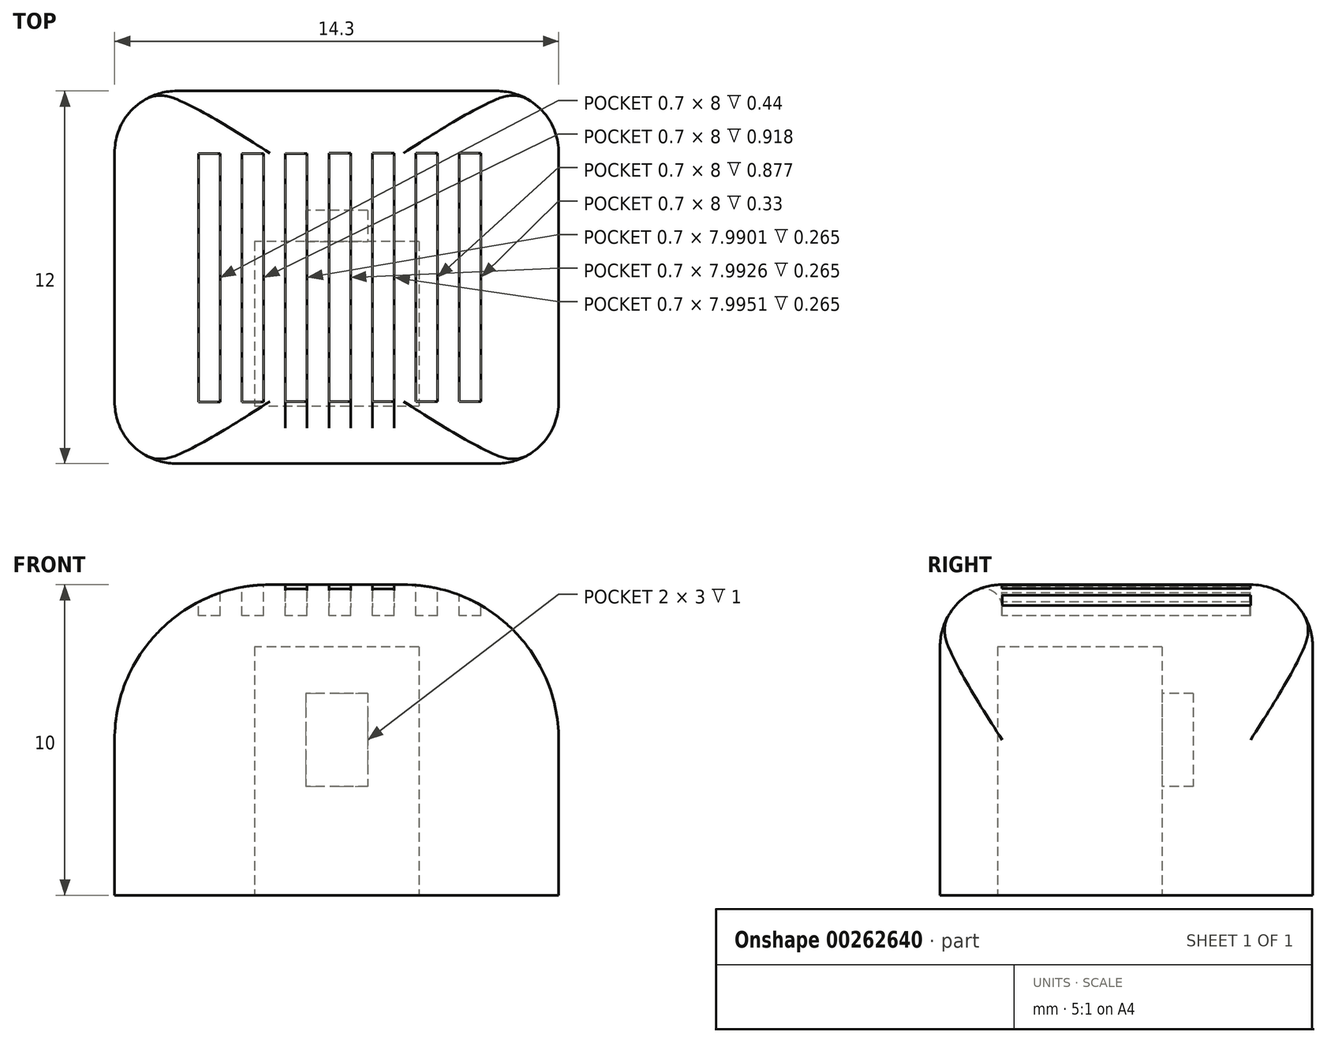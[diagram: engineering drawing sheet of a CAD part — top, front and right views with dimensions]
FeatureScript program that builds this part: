
annotation { "Feature Type Name" : "Feature", "Feature Type Description" : "" }
export const myFeature = defineFeature(function(context is Context, id is Id, definition is map)
    precondition{}
    {
        {
            var Q0;
            Q0=qCreatedBy(makeId("Top.planeOp"),FACE);
            var sketch = newSketch(context, id + "F0", { "sketchPlane" : qUnion([Q0])});
            skLineSegment(sketch, "E0", {"start": v(0, 0) * mm, "end": v(-7.15, 0) * mm});
            skLineSegment(sketch, "E1", {"start": v(-7.15, 0) * mm, "end": v(-7.15, 12) * mm});
            skLineSegment(sketch, "E2", {"start": v(-7.15, 12) * mm, "end": v(0, 12) * mm});
            skLineSegment(sketch, "E3", {"start": v(0, 8.15) * mm, "end": v(-1, 8.15) * mm});
            skLineSegment(sketch, "E4", {"start": v(-1, 8.15) * mm, "end": v(-1, 7.15) * mm});
            skLineSegment(sketch, "E5", {"start": v(-1, 7.15) * mm, "end": v(-2.65, 7.15) * mm});
            skLineSegment(sketch, "E6", {"start": v(-2.65, 7.15) * mm, "end": v(-2.65, 1.85) * mm});
            skLineSegment(sketch, "E7", {"start": v(-2.65, 1.85) * mm, "end": v(0, 1.85) * mm});
            skLineSegment(sketch, "E8", {"start": v(0, 12) * mm, "end": v(0, 8.15) * mm});
            skLineSegment(sketch, "E9", {"start": v(0, 1.85) * mm, "end": v(0, 8.15) * mm});
            skLineSegment(sketch, "E10", {"start": v(0, 1.85) * mm, "end": v(0, 0) * mm});
            skLineSegment(sketch, "E11", {"start": v(-1, 7.15) * mm, "end": v(0, 7.15) * mm});
            skSolve(sketch);
        }
        {
            var Q0;
            Q0=makeQuery(id+"F0.imprint","IMPRINT",FACE,{"disambiguationData":[TD([[makeQuery(id+"F0.imprint","IMPRINT",EDGE,{"derivedFrom":sQuery(id+"F0.wireOp",EDGE,"E0")}),-1.0]])]});
            var Q1;
            {var subQ2=sQuery(id+"F0.wireOp",EDGE,"E3");Q1=makeQuery(id+"F0.imprint","IMPRINT",FACE,{"disambiguationData":[TD([[makeQuery(id+"F0.imprint","IMPRINT",EDGE,{"derivedFrom":subQ2}),1.0]])]});}
            var Q2;
            Q2=makeQuery(id+"F0.imprint","IMPRINT",FACE,{"disambiguationData":[TD([[makeQuery(id+"F0.imprint","IMPRINT",EDGE,{"derivedFrom":sQuery(id+"F0.wireOp",EDGE,"E5")}),1.0]])]});
            extrude(context, id + "F1", {"entities" : qUnion([Q0, Q1, Q2]), "depth" : 10 * mm});
        }
        {
            var Q0;
            {var subQ2=sQuery(id+"F0.wireOp",EDGE,"E3");Q0=makeQuery(id+"F0.imprint","IMPRINT",FACE,{"disambiguationData":[TD([[makeQuery(id+"F0.imprint","IMPRINT",EDGE,{"derivedFrom":subQ2}),1.0]])]});}
            var Q1;
            Q1=makeQuery(id+"F0.imprint","IMPRINT",FACE,{"disambiguationData":[TD([[makeQuery(id+"F0.imprint","IMPRINT",EDGE,{"derivedFrom":sQuery(id+"F0.wireOp",EDGE,"E5")}),1.0]])]});
            extrude(context, id + "F2", {"entities" : qUnion([Q0, Q1]), "operationType" : NewBodyOperationType.REMOVE, "depth" : 8 * mm});
        }
        {
            var Q0;
            Q0=makeQuery(id+"F1.opExtrude","SWEPT_EDGE",EDGE,{"disambiguationData":[OSD([sQuery(id+"F0.wireOp",EDGE,"E0"),sQuery(id+"F0.wireOp",EDGE,"E1")])]});
            var Q1;
            Q1=makeQuery(id+"F1.opExtrude","CAP_EDGE",EDGE,{"disambiguationData":[OSD([sQuery(id+"F0.wireOp",EDGE,"E1")])],"isStart":false});
            var Q2;
            Q2=makeQuery(id+"F1.opExtrude","CAP_EDGE",EDGE,{"disambiguationData":[OSD([sQuery(id+"F0.wireOp",EDGE,"E0")])],"isStart":false});
            var Q3;
            Q3=makeQuery(id+"F1.opExtrude","CAP_EDGE",EDGE,{"disambiguationData":[OSD([sQuery(id+"F0.wireOp",EDGE,"E2")])],"isStart":false});
            var Q4;
            Q4=makeQuery(id+"F1.opExtrude","SWEPT_EDGE",EDGE,{"disambiguationData":[OSD([sQuery(id+"F0.wireOp",EDGE,"E1"),sQuery(id+"F0.wireOp",EDGE,"E2")])]});
            fillet(context, id + "F3", {"entities" : qUnion([Q0, Q1, Q2, Q3, Q4]), "radius" : 2 * mm, "tangentPropagation" : true, "allowEdgeOverflow" : false});
        }
        {
            var Q0;
            Q0=makeQuery(id+"F1.opExtrude","SWEPT_BODY",BODY,{"disambiguationData":[OSD([sQuery(id+"F0.wireOp",EDGE,"E0"),sQuery(id+"F0.wireOp",EDGE,"E1"),sQuery(id+"F0.wireOp",EDGE,"E2"),sQuery(id+"F0.wireOp",EDGE,"E8"),sQuery(id+"F0.wireOp",EDGE,"E9"),sQuery(id+"F0.wireOp",EDGE,"E10")])]});
            var Q1;
            Q1=qCreatedBy(makeId("Right.planeOp"),FACE);
            mirror(context, id + "F4", {"entities" : qUnion([Q0]), "mirrorPlane" : qUnion([Q1])});
        }
        {
            var Q0;
            Q0=makeQuery(id+"F1.opExtrude","SWEPT_BODY",BODY,{"disambiguationData":[OSD([sQuery(id+"F0.wireOp",EDGE,"E0"),sQuery(id+"F0.wireOp",EDGE,"E1"),sQuery(id+"F0.wireOp",EDGE,"E2"),sQuery(id+"F0.wireOp",EDGE,"E8"),sQuery(id+"F0.wireOp",EDGE,"E9"),sQuery(id+"F0.wireOp",EDGE,"E10")])]});
            var Q1;
            Q1=makeQuery(id+"F4.opPattern","COPY",BODY,{"derivedFrom":makeQuery(id+"F1.opExtrude","SWEPT_BODY",BODY,{"disambiguationData":[OSD([sQuery(id+"F0.wireOp",EDGE,"E0"),sQuery(id+"F0.wireOp",EDGE,"E1"),sQuery(id+"F0.wireOp",EDGE,"E2"),sQuery(id+"F0.wireOp",EDGE,"E8"),sQuery(id+"F0.wireOp",EDGE,"E9"),sQuery(id+"F0.wireOp",EDGE,"E10")])]}),"instanceName":"1"});
            booleanBodies(context, id + "F5", {"operationType" : BooleanOperationType.UNION, "tools" : qUnion([Q0, Q1])});
        }
        {
            var Q0;
            Q0=makeQuery(id+"F2.boolean.opBoolean","COPY",FACE,{"derivedFrom":makeQuery(id+"F2.opExtrude","SWEPT_FACE",FACE,{"disambiguationData":[OSD([sQuery(id+"F0.wireOp",EDGE,"E5")])]})});
            var sketch = newSketch(context, id + "F6", { "sketchPlane" : qUnion([Q0])});
            skLineSegment(sketch, "E12.0.0", {"start": v(1, 0) * mm, "end": v(-1, 0) * mm});
            skLineSegment(sketch, "E12.0.1", {"start": v(1, 8) * mm, "end": v(1, 0) * mm});
            skLineSegment(sketch, "E12.0.2", {"start": v(1, 8) * mm, "end": v(-1, 8) * mm});
            skLineSegment(sketch, "E12.0.3", {"start": v(-1, 8) * mm, "end": v(-1, 0) * mm});
            skLineSegment(sketch, "E13.bottom", {"start": v(-1, 6.5) * mm, "end": v(1, 6.5) * mm});
            skLineSegment(sketch, "E13.top", {"start": v(-1, 3.5) * mm, "end": v(1, 3.5) * mm});
            skLineSegment(sketch, "E13.left", {"start": v(-1, 6.5) * mm, "end": v(-1, 3.5) * mm});
            skLineSegment(sketch, "E13.right", {"start": v(1, 6.5) * mm, "end": v(1, 3.5) * mm});
            skSolve(sketch);
        }
        {
            var Q0;
            {var subQ0=makeQuery(id+"F1.opExtrude","SWEPT_FACE",FACE,{"disambiguationData":[OSD([sQuery(id+"F0.wireOp",EDGE,"E0")])]});Q0=makeQuery(id+"F5.opBoolean","MERGE",FACE,{"derivedFrom":[subQ0,makeQuery(id+"F4.opPattern","COPY",FACE,{"derivedFrom":subQ0,"instanceName":"1"})]});}
            var sketch = newSketch(context, id + "F7", { "sketchPlane" : qUnion([Q0])});
            skLineSegment(sketch, "E14.0", {"start": v(-7.15, 8) * mm, "end": v(-6.15, 8) * mm});
            skLineSegment(sketch, "E15.0", {"start": v(-7.15, 0) * mm, "end": v(-7.15, 5) * mm});
            skLineSegment(sketch, "E16.0.0", {"start": v(5.15, 0) * mm, "end": v(7.15, 0) * mm});
            skLineSegment(sketch, "E16.0.1", {"start": v(7.15, 0) * mm, "end": v(7.15, 8) * mm});
            skLineSegment(sketch, "E16.0.2", {"start": v(7.15, 8) * mm, "end": v(6.15, 8) * mm});
            skLineSegment(sketch, "E17.0", {"start": v(5.15, 9) * mm, "end": v(5.15, 10) * mm});
            skLineSegment(sketch, "E18.0", {"start": v(-5.15, 9) * mm, "end": v(-5.15, 10) * mm});
            skLineSegment(sketch, "E19", {"start": v(-2.15, 10) * mm, "end": v(5.15, 10) * mm});
            skLineSegment(sketch, "E20", {"start": v(5.15, 10) * mm, "end": v(7.15, 10) * mm});
            skLineSegment(sketch, "E21", {"start": v(7.15, 10) * mm, "end": v(7.15, 8) * mm});
            skLineSegment(sketch, "E22", {"start": v(-7.15, 8) * mm, "end": v(-7.15, 10) * mm});
            skLineSegment(sketch, "E23", {"start": v(-7.15, 10) * mm, "end": v(-5.15, 10) * mm});
            skArc(sketch, "E24.filletArc", {"start": v(-2.15, 10) * mm, "mid": v(-5.69, 8.54) * mm, "end": v(-7.15, 5) * mm});
            skArc(sketch, "E25.0.MirrorCS", {"start": v(2.15, 10) * mm, "mid": v(5.69, 8.54) * mm, "end": v(7.15, 5) * mm});
            skPoint(sketch, "E26.0.end.orphan", {"position": v(-5.15, 8) * mm});
            skPoint(sketch, "E27.orphan", {"position": v(5.15, 8) * mm});
            skLineSegment(sketch, "E28", {"start": v(-7.15, 0) * mm, "end": v(5.15, 0) * mm});
            skPoint(sketch, "E29.start.orphan", {"position": v(0, 0) * mm});
            skSolve(sketch);
        }
        {
            var Q0;
            {var subQ5=sQuery(id+"F7.wireOp",EDGE,"E15.0");Q0=makeQuery(id+"F7.imprint","IMPRINT",FACE,{"disambiguationData":[TD([[makeQuery(id+"F7.imprint","IMPRINT",EDGE,{"derivedFrom":subQ5}),-1.0]])]});}
            var Q1;
            {var subQ0=sQuery(id+"F0.wireOp",EDGE,"E0");var subQ1=makeQuery(id+"F1.opExtrude","SWEPT_FACE",FACE,{"disambiguationData":[OSD([subQ0])]});var subQ3=makeQuery(id+"F3.opFillet","BLEND_EDGE",EDGE,{"blendedFrom":[makeQuery(id+"F1.opExtrude","SWEPT_EDGE",EDGE,{"disambiguationData":[OSD([subQ0,sQuery(id+"F0.wireOp",EDGE,"E1")])]}),subQ1],"blendedInto":[subQ1]});Q1=makeQuery(id+"F7.imprint","IMPRINT",FACE,{"disambiguationData":[TD([[makeQuery(id+"F7.imprint","IMPRINT",EDGE,{"derivedFrom":subQ3}),1.0]])]});}
            extrude(context, id + "F8", {"entities" : qUnion([Q0, Q1]), "operationType" : NewBodyOperationType.INTERSECT, "oppositeDirection" : true, "depth" : 25 * mm});
        }
        {
            var Q0;
            {var subQ2=sQuery(id+"F6.wireOp",EDGE,"E12.0.0");Q0=makeQuery(id+"F6.imprint","IMPRINT",FACE,{"disambiguationData":[TD([[makeQuery(id+"F6.imprint","IMPRINT",EDGE,{"derivedFrom":subQ2}),-1.0]])]});}
            var Q1;
            {var subQ2=sQuery(id+"F6.wireOp",EDGE,"E12.0.2");Q1=makeQuery(id+"F6.imprint","IMPRINT",FACE,{"disambiguationData":[TD([[makeQuery(id+"F6.imprint","IMPRINT",EDGE,{"derivedFrom":subQ2}),1.0]])]});}
            var Q2;
            {var subQ0=makeQuery(id+"F2.boolean.opBoolean","COPY",FACE,{"derivedFrom":makeQuery(id+"F2.opExtrude","SWEPT_FACE",FACE,{"disambiguationData":[OSD([sQuery(id+"F0.wireOp",EDGE,"E3")])]})});Q2=makeQuery(id+"F5.opBoolean","MERGE",FACE,{"derivedFrom":[subQ0,makeQuery(id+"F4.opPattern","COPY",FACE,{"derivedFrom":subQ0,"instanceName":"1"})]});}
            extrude(context, id + "F9", {"entities" : qUnion([Q0, Q1]), "operationType" : NewBodyOperationType.ADD, "endBound" : BoundingType.UP_TO_SURFACE, "oppositeDirection" : true, "endBoundEntityFace" : qUnion([Q2]), "depth" : 25 * mm});
        }
        {
            var Q0;
            {var subQ0=makeQuery(id+"F1.opExtrude","CAP_FACE",FACE,{"disambiguationData":[OSD([sQuery(id+"F0.wireOp",EDGE,"E0"),sQuery(id+"F0.wireOp",EDGE,"E1"),sQuery(id+"F0.wireOp",EDGE,"E2"),sQuery(id+"F0.wireOp",EDGE,"E8"),sQuery(id+"F0.wireOp",EDGE,"E9"),sQuery(id+"F0.wireOp",EDGE,"E10")])],"isStart":false});Q0=makeQuery(id+"F5.opBoolean","MERGE",FACE,{"derivedFrom":[subQ0,makeQuery(id+"F4.opPattern","COPY",FACE,{"derivedFrom":subQ0,"instanceName":"1"})]});}
            var sketch = newSketch(context, id + "F10", { "sketchPlane" : qUnion([Q0])});
            skLineSegment(sketch, "E30.0.MirrorCS", {"start": v(3.95, 10) * mm, "end": v(3.95, 2) * mm});
            skLineSegment(sketch, "E31.0.MirrorCS", {"start": v(4.65, 10) * mm, "end": v(4.65, 2) * mm});
            skLineSegment(sketch, "E32", {"start": v(4.65, 10) * mm, "end": v(3.95, 10) * mm});
            skLineSegment(sketch, "E33", {"start": v(4.65, 2) * mm, "end": v(3.95, 2) * mm});
            skLineSegment(sketch, "E34.1.0.0", {"start": v(3.25, 2) * mm, "end": v(2.55, 2) * mm});
            skLineSegment(sketch, "E34.1.0.1", {"start": v(3.25, 10) * mm, "end": v(3.25, 2) * mm});
            skLineSegment(sketch, "E34.1.0.2", {"start": v(2.55, 10) * mm, "end": v(2.55, 2) * mm});
            skLineSegment(sketch, "E34.1.0.3", {"start": v(3.25, 10) * mm, "end": v(2.55, 10) * mm});
            skLineSegment(sketch, "E34.2.0.0", {"start": v(1.85, 2) * mm, "end": v(1.15, 2) * mm});
            skLineSegment(sketch, "E34.2.0.1", {"start": v(1.85, 10) * mm, "end": v(1.85, 2) * mm});
            skLineSegment(sketch, "E34.2.0.2", {"start": v(1.15, 10) * mm, "end": v(1.15, 2) * mm});
            skLineSegment(sketch, "E34.2.0.3", {"start": v(1.85, 10) * mm, "end": v(1.15, 10) * mm});
            skLineSegment(sketch, "E34.3.0.0", {"start": v(0.45, 2) * mm, "end": v(-0.25, 2) * mm});
            skLineSegment(sketch, "E34.3.0.1", {"start": v(0.45, 10) * mm, "end": v(0.45, 2) * mm});
            skLineSegment(sketch, "E34.3.0.2", {"start": v(-0.25, 10) * mm, "end": v(-0.25, 2) * mm});
            skLineSegment(sketch, "E34.3.0.3", {"start": v(0.45, 10) * mm, "end": v(-0.25, 10) * mm});
            skLineSegment(sketch, "E34.4.0.0", {"start": v(-0.95, 2) * mm, "end": v(-1.65, 2) * mm});
            skLineSegment(sketch, "E34.4.0.1", {"start": v(-0.95, 10) * mm, "end": v(-0.95, 2) * mm});
            skLineSegment(sketch, "E34.4.0.2", {"start": v(-1.65, 10) * mm, "end": v(-1.65, 2) * mm});
            skLineSegment(sketch, "E34.4.0.3", {"start": v(-0.95, 10) * mm, "end": v(-1.65, 10) * mm});
            skLineSegment(sketch, "E34.5.0.0", {"start": v(-2.35, 1.99) * mm, "end": v(-3.05, 1.99) * mm});
            skLineSegment(sketch, "E34.5.0.1", {"start": v(-2.35, 9.99) * mm, "end": v(-2.35, 1.99) * mm});
            skLineSegment(sketch, "E34.5.0.2", {"start": v(-3.05, 9.99) * mm, "end": v(-3.05, 1.99) * mm});
            skLineSegment(sketch, "E34.5.0.3", {"start": v(-2.35, 9.99) * mm, "end": v(-3.05, 9.99) * mm});
            skLineSegment(sketch, "E34.6.0.0", {"start": v(-3.75, 1.99) * mm, "end": v(-4.45, 1.99) * mm});
            skLineSegment(sketch, "E34.6.0.1", {"start": v(-3.75, 9.99) * mm, "end": v(-3.75, 1.99) * mm});
            skLineSegment(sketch, "E34.6.0.2", {"start": v(-4.45, 9.99) * mm, "end": v(-4.45, 1.99) * mm});
            skLineSegment(sketch, "E34.6.0.3", {"start": v(-3.75, 9.99) * mm, "end": v(-4.45, 9.99) * mm});
            skLineSegment(sketch, "E34.direction1", {"start": v(3.95, 2) * mm, "end": v(2.55, 2) * mm, "construction": true});
            skSolve(sketch);
        }
        {
            var Q0;
            Q0=makeQuery(id+"F10.imprint","IMPRINT",FACE,{"disambiguationData":[TD([[makeQuery(id+"F10.imprint","IMPRINT",EDGE,{"derivedFrom":sQuery(id+"F10.wireOp",EDGE,"E30.0.MirrorCS")}),1.0]])]});
            var Q1;
            Q1=makeQuery(id+"F10.imprint","IMPRINT",FACE,{"disambiguationData":[TD([[makeQuery(id+"F10.imprint","IMPRINT",EDGE,{"derivedFrom":sQuery(id+"F10.wireOp",EDGE,"E34.1.0.0")}),-1.0]])]});
            var Q2;
            {var subQ0=sQuery(id+"F10.wireOp",EDGE,"E34.2.0.3");Q2=makeQuery(id+"F10.imprint","IMPRINT",FACE,{"disambiguationData":[TD([[makeQuery(id+"F10.imprint","IMPRINT",EDGE,{"derivedFrom":subQ0}),1.0]])]});}
            var Q3;
            {var subQ0=sQuery(id+"F10.wireOp",EDGE,"E34.3.0.3");Q3=makeQuery(id+"F10.imprint","IMPRINT",FACE,{"disambiguationData":[TD([[makeQuery(id+"F10.imprint","IMPRINT",EDGE,{"derivedFrom":subQ0}),1.0]])]});}
            var Q4;
            {var subQ0=sQuery(id+"F10.wireOp",EDGE,"E34.4.0.3");Q4=makeQuery(id+"F10.imprint","IMPRINT",FACE,{"disambiguationData":[TD([[makeQuery(id+"F10.imprint","IMPRINT",EDGE,{"derivedFrom":subQ0}),1.0]])]});}
            var Q5;
            Q5=makeQuery(id+"F10.imprint","IMPRINT",FACE,{"disambiguationData":[TD([[makeQuery(id+"F10.imprint","IMPRINT",EDGE,{"derivedFrom":sQuery(id+"F10.wireOp",EDGE,"E34.5.0.0")}),-1.0]])]});
            var Q6;
            Q6=makeQuery(id+"F10.imprint","IMPRINT",FACE,{"disambiguationData":[TD([[makeQuery(id+"F10.imprint","IMPRINT",EDGE,{"derivedFrom":sQuery(id+"F10.wireOp",EDGE,"E34.6.0.0")}),-1.0]])]});
            extrude(context, id + "F11", {"entities" : qUnion([Q0, Q1, Q2, Q3, Q4, Q5, Q6]), "operationType" : NewBodyOperationType.REMOVE, "oppositeDirection" : true, "depth" : 1 * mm});
        }
        {
            var Q0;
            Q0=makeQuery(id+"F11.boolean.opBoolean","INTERSECT",EDGE,{"derivedFrom":[makeQuery(id+"F8.boolean.opBoolean","COPY",FACE,{"derivedFrom":makeQuery(id+"F8.boolean.toolComplement.opBoolean","COPY",FACE,{"derivedFrom":makeQuery(id+"F8.opExtrude","SWEPT_FACE",FACE,{"disambiguationData":[OSD([sQuery(id+"F7.wireOp",EDGE,"E24.filletArc")])]})})}),makeQuery(id+"F11.opExtrude","SWEPT_FACE",FACE,{"disambiguationData":[OSD([sQuery(id+"F10.wireOp",EDGE,"E34.6.0.2")])]})]});
            var Q1;
            Q1=makeQuery(id+"F11.boolean.opBoolean","INTERSECT",EDGE,{"derivedFrom":[makeQuery(id+"F8.boolean.opBoolean","COPY",FACE,{"derivedFrom":makeQuery(id+"F8.boolean.toolComplement.opBoolean","COPY",FACE,{"derivedFrom":makeQuery(id+"F8.opExtrude","SWEPT_FACE",FACE,{"disambiguationData":[OSD([sQuery(id+"F7.wireOp",EDGE,"E24.filletArc")])]})})}),makeQuery(id+"F11.opExtrude","SWEPT_FACE",FACE,{"disambiguationData":[OSD([sQuery(id+"F10.wireOp",EDGE,"E34.5.0.2")])]})]});
            var Q2;
            Q2=makeQuery(id+"F11.boolean.opBoolean","COPY",EDGE,{"derivedFrom":makeQuery(id+"F11.opExtrude","CAP_EDGE",EDGE,{"disambiguationData":[OSD([sQuery(id+"F10.wireOp",EDGE,"E34.4.0.2")])],"isStart":true})});
            var Q3;
            Q3=makeQuery(id+"F11.boolean.opBoolean","COPY",EDGE,{"derivedFrom":makeQuery(id+"F11.opExtrude","CAP_EDGE",EDGE,{"disambiguationData":[OSD([sQuery(id+"F10.wireOp",EDGE,"E34.3.0.2")])],"isStart":true})});
            var Q4;
            Q4=makeQuery(id+"F11.boolean.opBoolean","COPY",EDGE,{"derivedFrom":makeQuery(id+"F11.opExtrude","CAP_EDGE",EDGE,{"disambiguationData":[OSD([sQuery(id+"F10.wireOp",EDGE,"E34.2.0.2")])],"isStart":true})});
            var Q5;
            Q5=makeQuery(id+"F11.boolean.opBoolean","INTERSECT",EDGE,{"derivedFrom":[makeQuery(id+"F8.boolean.opBoolean","COPY",FACE,{"derivedFrom":makeQuery(id+"F8.boolean.toolComplement.opBoolean","COPY",FACE,{"derivedFrom":makeQuery(id+"F8.opExtrude","SWEPT_FACE",FACE,{"disambiguationData":[OSD([sQuery(id+"F7.wireOp",EDGE,"E25.0.MirrorCS")])]})})}),makeQuery(id+"F11.opExtrude","SWEPT_FACE",FACE,{"disambiguationData":[OSD([sQuery(id+"F10.wireOp",EDGE,"E34.1.0.2")])]})]});
            var Q6;
            Q6=makeQuery(id+"F11.boolean.opBoolean","INTERSECT",EDGE,{"derivedFrom":[makeQuery(id+"F8.boolean.opBoolean","COPY",FACE,{"derivedFrom":makeQuery(id+"F8.boolean.toolComplement.opBoolean","COPY",FACE,{"derivedFrom":makeQuery(id+"F8.opExtrude","SWEPT_FACE",FACE,{"disambiguationData":[OSD([sQuery(id+"F7.wireOp",EDGE,"E25.0.MirrorCS")])]})})}),makeQuery(id+"F11.opExtrude","SWEPT_FACE",FACE,{"disambiguationData":[OSD([sQuery(id+"F10.wireOp",EDGE,"E30.0.MirrorCS")])]})]});
            var Q7;
            Q7=makeQuery(id+"F11.boolean.opBoolean","INTERSECT",EDGE,{"derivedFrom":[makeQuery(id+"F8.boolean.opBoolean","COPY",FACE,{"derivedFrom":makeQuery(id+"F8.boolean.toolComplement.opBoolean","COPY",FACE,{"derivedFrom":makeQuery(id+"F8.opExtrude","SWEPT_FACE",FACE,{"disambiguationData":[OSD([sQuery(id+"F7.wireOp",EDGE,"E25.0.MirrorCS")])]})})}),makeQuery(id+"F11.opExtrude","SWEPT_FACE",FACE,{"disambiguationData":[OSD([sQuery(id+"F10.wireOp",EDGE,"E31.0.MirrorCS")])]})]});
            var Q8;
            Q8=makeQuery(id+"F11.boolean.opBoolean","INTERSECT",EDGE,{"derivedFrom":[makeQuery(id+"F8.boolean.opBoolean","COPY",FACE,{"derivedFrom":makeQuery(id+"F8.boolean.toolComplement.opBoolean","COPY",FACE,{"derivedFrom":makeQuery(id+"F8.opExtrude","SWEPT_FACE",FACE,{"disambiguationData":[OSD([sQuery(id+"F7.wireOp",EDGE,"E25.0.MirrorCS")])]})})}),makeQuery(id+"F11.opExtrude","SWEPT_FACE",FACE,{"disambiguationData":[OSD([sQuery(id+"F10.wireOp",EDGE,"E34.1.0.1")])]})]});
            var Q9;
            Q9=makeQuery(id+"F11.boolean.opBoolean","COPY",EDGE,{"derivedFrom":makeQuery(id+"F11.opExtrude","CAP_EDGE",EDGE,{"disambiguationData":[OSD([sQuery(id+"F10.wireOp",EDGE,"E34.2.0.1")])],"isStart":true})});
            var Q10;
            Q10=makeQuery(id+"F11.boolean.opBoolean","COPY",EDGE,{"derivedFrom":makeQuery(id+"F11.opExtrude","CAP_EDGE",EDGE,{"disambiguationData":[OSD([sQuery(id+"F10.wireOp",EDGE,"E34.3.0.1")])],"isStart":true})});
            var Q11;
            Q11=makeQuery(id+"F11.boolean.opBoolean","COPY",EDGE,{"derivedFrom":makeQuery(id+"F11.opExtrude","CAP_EDGE",EDGE,{"disambiguationData":[OSD([sQuery(id+"F10.wireOp",EDGE,"E34.4.0.1")])],"isStart":true})});
            var Q12;
            Q12=makeQuery(id+"F11.boolean.opBoolean","INTERSECT",EDGE,{"derivedFrom":[makeQuery(id+"F8.boolean.opBoolean","COPY",FACE,{"derivedFrom":makeQuery(id+"F8.boolean.toolComplement.opBoolean","COPY",FACE,{"derivedFrom":makeQuery(id+"F8.opExtrude","SWEPT_FACE",FACE,{"disambiguationData":[OSD([sQuery(id+"F7.wireOp",EDGE,"E24.filletArc")])]})})}),makeQuery(id+"F11.opExtrude","SWEPT_FACE",FACE,{"disambiguationData":[OSD([sQuery(id+"F10.wireOp",EDGE,"E34.5.0.1")])]})]});
            var Q13;
            Q13=makeQuery(id+"F8.boolean.opBoolean","COPY",FACE,{"derivedFrom":makeQuery(id+"F8.boolean.toolComplement.opBoolean","COPY",FACE,{"derivedFrom":makeQuery(id+"F8.opExtrude","SWEPT_FACE",FACE,{"disambiguationData":[OSD([sQuery(id+"F7.wireOp",EDGE,"E24.filletArc")])]})})});
            var Q14;
            Q14=makeQuery(id+"F11.boolean.opBoolean","COPY",EDGE,{"derivedFrom":makeQuery(id+"F11.opExtrude","CAP_EDGE",EDGE,{"disambiguationData":[OSD([sQuery(id+"F10.wireOp",EDGE,"E34.4.0.3")])],"isStart":true})});
            var Q15;
            {var subQ0=sQuery(id+"F0.wireOp",EDGE,"E10");var subQ1=sQuery(id+"F0.wireOp",EDGE,"E9");var subQ2=sQuery(id+"F0.wireOp",EDGE,"E8");var subQ3=sQuery(id+"F0.wireOp",EDGE,"E2");var subQ4=sQuery(id+"F0.wireOp",EDGE,"E1");var subQ5=sQuery(id+"F0.wireOp",EDGE,"E0");var subQ6=makeQuery(id+"F3.opFillet","BLEND_EDGE",EDGE,{"blendedFrom":[makeQuery(id+"F1.opExtrude","CAP_EDGE",EDGE,{"disambiguationData":[OSD([subQ5])],"isStart":false}),makeQuery(id+"F1.opExtrude","CAP_FACE",FACE,{"disambiguationData":[OSD([subQ5,subQ4,subQ3,subQ2,subQ1,subQ0])],"isStart":false})],"blendedInto":[makeQuery(id+"F1.opExtrude","CAP_FACE",FACE,{"disambiguationData":[OSD([subQ5,subQ4,subQ3,subQ2,subQ1,subQ0])],"isStart":false})]});var subQ7=makeQuery(id+"F5.opBoolean","MERGE",EDGE,{"derivedFrom":[subQ6,makeQuery(id+"F4.opPattern","COPY",EDGE,{"derivedFrom":subQ6,"instanceName":"1"})]});Q15=makeQuery(id+"F11.boolean.opBoolean","MERGE",EDGE,{"derivedFrom":[subQ7,makeQuery(id+"F11.opExtrude","CAP_EDGE",EDGE,{"disambiguationData":[OSD([subQ5,subQ4,subQ3,subQ2,subQ1,subQ0]),TDD([makeQuery(id+"F10.imprint","IMPRINT",EDGE,{"disambiguationData":[TD([[makeQuery(id+"F10.imprint","INTERSECT",VERTEX,{"derivedFrom":[subQ7,sQuery(id+"F10.wireOp",EDGE,"E34.4.0.1")]}),1.0]])],"derivedFrom":subQ7})])],"isStart":true})]});}
            var Q16;
            {var subQ0=sQuery(id+"F0.wireOp",EDGE,"E10");var subQ1=sQuery(id+"F0.wireOp",EDGE,"E9");var subQ2=sQuery(id+"F0.wireOp",EDGE,"E8");var subQ3=sQuery(id+"F0.wireOp",EDGE,"E2");var subQ4=sQuery(id+"F0.wireOp",EDGE,"E1");var subQ5=sQuery(id+"F0.wireOp",EDGE,"E0");var subQ6=makeQuery(id+"F3.opFillet","BLEND_EDGE",EDGE,{"blendedFrom":[makeQuery(id+"F1.opExtrude","CAP_EDGE",EDGE,{"disambiguationData":[OSD([subQ5])],"isStart":false}),makeQuery(id+"F1.opExtrude","CAP_FACE",FACE,{"disambiguationData":[OSD([subQ5,subQ4,subQ3,subQ2,subQ1,subQ0])],"isStart":false})],"blendedInto":[makeQuery(id+"F1.opExtrude","CAP_FACE",FACE,{"disambiguationData":[OSD([subQ5,subQ4,subQ3,subQ2,subQ1,subQ0])],"isStart":false})]});var subQ7=makeQuery(id+"F5.opBoolean","MERGE",EDGE,{"derivedFrom":[subQ6,makeQuery(id+"F4.opPattern","COPY",EDGE,{"derivedFrom":subQ6,"instanceName":"1"})]});Q16=makeQuery(id+"F11.boolean.opBoolean","MERGE",EDGE,{"derivedFrom":[subQ7,makeQuery(id+"F11.opExtrude","CAP_EDGE",EDGE,{"disambiguationData":[OSD([subQ5,subQ4,subQ3,subQ2,subQ1,subQ0]),TDD([makeQuery(id+"F10.imprint","IMPRINT",EDGE,{"disambiguationData":[TD([[makeQuery(id+"F10.imprint","INTERSECT",VERTEX,{"derivedFrom":[subQ7,sQuery(id+"F10.wireOp",EDGE,"E34.3.0.1")]}),1.0]])],"derivedFrom":subQ7})])],"isStart":true})]});}
            var Q17;
            Q17=makeQuery(id+"F11.boolean.opBoolean","COPY",EDGE,{"derivedFrom":makeQuery(id+"F11.opExtrude","CAP_EDGE",EDGE,{"disambiguationData":[OSD([sQuery(id+"F10.wireOp",EDGE,"E34.3.0.3")])],"isStart":true})});
            var Q18;
            Q18=makeQuery(id+"F11.boolean.opBoolean","COPY",EDGE,{"derivedFrom":makeQuery(id+"F11.opExtrude","CAP_EDGE",EDGE,{"disambiguationData":[OSD([sQuery(id+"F10.wireOp",EDGE,"E34.2.0.3")])],"isStart":true})});
            var Q19;
            {var subQ0=sQuery(id+"F0.wireOp",EDGE,"E10");var subQ1=sQuery(id+"F0.wireOp",EDGE,"E9");var subQ2=sQuery(id+"F0.wireOp",EDGE,"E8");var subQ3=sQuery(id+"F0.wireOp",EDGE,"E2");var subQ4=sQuery(id+"F0.wireOp",EDGE,"E1");var subQ5=sQuery(id+"F0.wireOp",EDGE,"E0");var subQ6=makeQuery(id+"F3.opFillet","BLEND_EDGE",EDGE,{"blendedFrom":[makeQuery(id+"F1.opExtrude","CAP_EDGE",EDGE,{"disambiguationData":[OSD([subQ5])],"isStart":false}),makeQuery(id+"F1.opExtrude","CAP_FACE",FACE,{"disambiguationData":[OSD([subQ5,subQ4,subQ3,subQ2,subQ1,subQ0])],"isStart":false})],"blendedInto":[makeQuery(id+"F1.opExtrude","CAP_FACE",FACE,{"disambiguationData":[OSD([subQ5,subQ4,subQ3,subQ2,subQ1,subQ0])],"isStart":false})]});var subQ7=makeQuery(id+"F5.opBoolean","MERGE",EDGE,{"derivedFrom":[subQ6,makeQuery(id+"F4.opPattern","COPY",EDGE,{"derivedFrom":subQ6,"instanceName":"1"})]});Q19=makeQuery(id+"F11.boolean.opBoolean","MERGE",EDGE,{"derivedFrom":[subQ7,makeQuery(id+"F11.opExtrude","CAP_EDGE",EDGE,{"disambiguationData":[OSD([subQ5,subQ4,subQ3,subQ2,subQ1,subQ0]),TDD([makeQuery(id+"F10.imprint","IMPRINT",EDGE,{"disambiguationData":[TD([[makeQuery(id+"F10.imprint","INTERSECT",VERTEX,{"derivedFrom":[subQ7,sQuery(id+"F10.wireOp",EDGE,"E34.2.0.1")]}),1.0]])],"derivedFrom":subQ7})])],"isStart":true})]});}
            var Q20;
            Q20=makeQuery(id+"F11.boolean.opBoolean","INTERSECT",EDGE,{"derivedFrom":[makeQuery(id+"F8.boolean.opBoolean","COPY",FACE,{"derivedFrom":makeQuery(id+"F8.boolean.toolComplement.opBoolean","COPY",FACE,{"derivedFrom":makeQuery(id+"F8.opExtrude","SWEPT_FACE",FACE,{"disambiguationData":[OSD([sQuery(id+"F7.wireOp",EDGE,"E25.0.MirrorCS")])]})})}),makeQuery(id+"F11.opExtrude","SWEPT_FACE",FACE,{"disambiguationData":[OSD([sQuery(id+"F10.wireOp",EDGE,"E34.1.0.0")])]})]});
            var Q21;
            Q21=makeQuery(id+"F11.boolean.opBoolean","INTERSECT",EDGE,{"derivedFrom":[makeQuery(id+"F8.boolean.opBoolean","COPY",FACE,{"derivedFrom":makeQuery(id+"F8.boolean.toolComplement.opBoolean","COPY",FACE,{"derivedFrom":makeQuery(id+"F8.opExtrude","SWEPT_FACE",FACE,{"disambiguationData":[OSD([sQuery(id+"F7.wireOp",EDGE,"E25.0.MirrorCS")])]})})}),makeQuery(id+"F11.opExtrude","SWEPT_FACE",FACE,{"disambiguationData":[OSD([sQuery(id+"F10.wireOp",EDGE,"E33")])]})]});
            var Q22;
            Q22=makeQuery(id+"F11.boolean.opBoolean","INTERSECT",EDGE,{"derivedFrom":[makeQuery(id+"F8.boolean.opBoolean","COPY",FACE,{"derivedFrom":makeQuery(id+"F8.boolean.toolComplement.opBoolean","COPY",FACE,{"derivedFrom":makeQuery(id+"F8.opExtrude","SWEPT_FACE",FACE,{"disambiguationData":[OSD([sQuery(id+"F7.wireOp",EDGE,"E25.0.MirrorCS")])]})})}),makeQuery(id+"F11.opExtrude","SWEPT_FACE",FACE,{"disambiguationData":[OSD([sQuery(id+"F10.wireOp",EDGE,"E32")])]})]});
            var Q23;
            Q23=makeQuery(id+"F11.boolean.opBoolean","INTERSECT",EDGE,{"derivedFrom":[makeQuery(id+"F8.boolean.opBoolean","COPY",FACE,{"derivedFrom":makeQuery(id+"F8.boolean.toolComplement.opBoolean","COPY",FACE,{"derivedFrom":makeQuery(id+"F8.opExtrude","SWEPT_FACE",FACE,{"disambiguationData":[OSD([sQuery(id+"F7.wireOp",EDGE,"E25.0.MirrorCS")])]})})}),makeQuery(id+"F11.opExtrude","SWEPT_FACE",FACE,{"disambiguationData":[OSD([sQuery(id+"F10.wireOp",EDGE,"E34.1.0.3")])]})]});
            fillet(context, id + "F12", {"entities" : qUnion([Q0, Q1, Q2, Q3, Q4, Q5, Q6, Q7, Q8, Q9, Q10, Q11, Q12, Q13, Q14, Q15, Q16, Q17, Q18, Q19, Q20, Q21, Q22, Q23]), "radius" : .6 * mm, "allowEdgeOverflow" : false});
        }
    });
